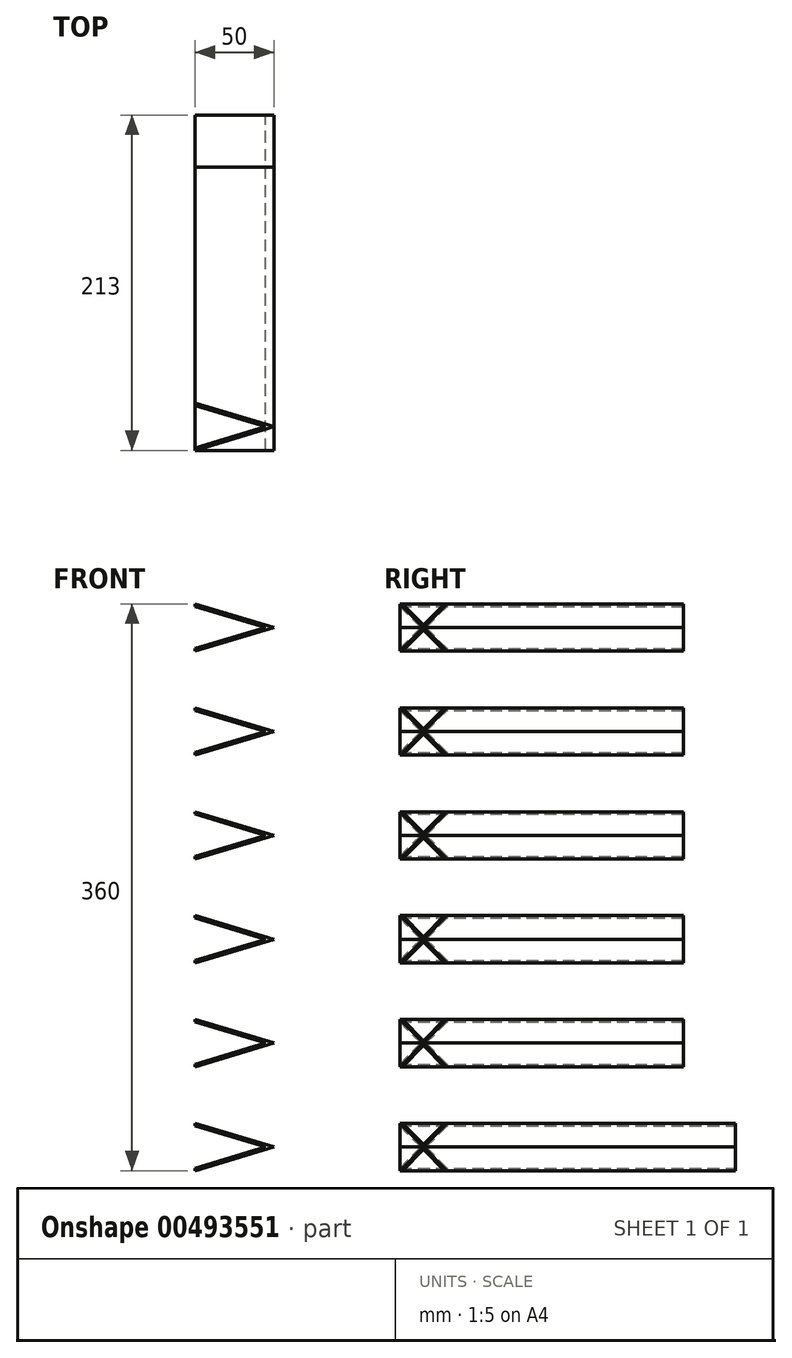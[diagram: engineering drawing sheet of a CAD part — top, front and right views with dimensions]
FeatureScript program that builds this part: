
annotation { "Feature Type Name" : "Feature", "Feature Type Description" : "" }
export const myFeature = defineFeature(function(context is Context, id is Id, definition is map)
    precondition{}
    {
        {
            var Q0;
            Q0=qCreatedBy(makeId("Right.planeOp"),FACE);
            var sketch = newSketch(context, id + "F0", { "sketchPlane" : qUnion([Q0])});
            skLineSegment(sketch, "E0", {"start": v(0, 0) * mm, "end": v(0, 400) * mm});
            skLineSegment(sketch, "E1", {"start": v(0, 0) * mm, "end": v(100, 0) * mm});
            skLineSegment(sketch, "E2", {"start": v(100, 0) * mm, "end": v(100, 360) * mm});
            skLineSegment(sketch, "E3.bottom", {"start": v(100, 360) * mm, "end": v(130, 360) * mm});
            skLineSegment(sketch, "E3.top", {"start": v(100, 0) * mm, "end": v(130, 0) * mm});
            skLineSegment(sketch, "E3.left", {"start": v(100, 360) * mm, "end": v(100, 0) * mm});
            skLineSegment(sketch, "E3.right", {"start": v(130, 360) * mm, "end": v(130, 0) * mm});
            skLineSegment(sketch, "E4.bottom", {"start": v(130, 0) * mm, "end": v(280, 0) * mm});
            skLineSegment(sketch, "E4.top", {"start": v(100, 30) * mm, "end": v(280, 30) * mm});
            skLineSegment(sketch, "E4.left", {"start": v(130, 0) * mm, "end": v(130, 30) * mm});
            skLineSegment(sketch, "E4.right", {"start": v(280, 0) * mm, "end": v(280, 30) * mm});
            skLineSegment(sketch, "E5", {"start": v(280, 66) * mm, "end": v(130, 66) * mm});
            skLineSegment(sketch, "E6", {"start": v(280, 66) * mm, "end": v(280, 96) * mm});
            skLineSegment(sketch, "E7.bottom", {"start": v(280, 96) * mm, "end": v(130, 96) * mm});
            skLineSegment(sketch, "E7.left", {"start": v(280, 96) * mm, "end": v(280, 66) * mm});
            skLineSegment(sketch, "E7.right", {"start": v(130, 96) * mm, "end": v(130, 66) * mm});
            skLineSegment(sketch, "E8.0.1.0", {"start": v(280, 132) * mm, "end": v(130, 132) * mm});
            skLineSegment(sketch, "E8.0.1.1", {"start": v(280, 132) * mm, "end": v(280, 162) * mm});
            skLineSegment(sketch, "E8.0.1.2", {"start": v(130, 162) * mm, "end": v(130, 132) * mm});
            skLineSegment(sketch, "E8.0.1.3", {"start": v(280, 162) * mm, "end": v(130, 162) * mm});
            skLineSegment(sketch, "E8.0.1.4", {"start": v(280, 162) * mm, "end": v(280, 132) * mm});
            skLineSegment(sketch, "E8.0.1.5", {"start": v(280, 132) * mm, "end": v(130, 132) * mm});
            skLineSegment(sketch, "E8.0.2.0", {"start": v(280, 198) * mm, "end": v(130, 198) * mm});
            skLineSegment(sketch, "E8.0.2.1", {"start": v(280, 198) * mm, "end": v(280, 228) * mm});
            skLineSegment(sketch, "E8.0.2.2", {"start": v(130, 228) * mm, "end": v(130, 198) * mm});
            skLineSegment(sketch, "E8.0.2.3", {"start": v(280, 228) * mm, "end": v(130, 228) * mm});
            skLineSegment(sketch, "E8.0.2.4", {"start": v(280, 228) * mm, "end": v(280, 198) * mm});
            skLineSegment(sketch, "E8.0.2.5", {"start": v(280, 198) * mm, "end": v(130, 198) * mm});
            skLineSegment(sketch, "E8.0.3.0", {"start": v(280, 264) * mm, "end": v(130, 264) * mm});
            skLineSegment(sketch, "E8.0.3.1", {"start": v(280, 264) * mm, "end": v(280, 294) * mm});
            skLineSegment(sketch, "E8.0.3.2", {"start": v(130, 294) * mm, "end": v(130, 264) * mm});
            skLineSegment(sketch, "E8.0.3.3", {"start": v(280, 294) * mm, "end": v(130, 294) * mm});
            skLineSegment(sketch, "E8.0.3.4", {"start": v(280, 294) * mm, "end": v(280, 264) * mm});
            skLineSegment(sketch, "E8.0.3.5", {"start": v(280, 264) * mm, "end": v(130, 264) * mm});
            skLineSegment(sketch, "E8.0.4.0", {"start": v(280, 330) * mm, "end": v(100, 330) * mm});
            skLineSegment(sketch, "E8.0.4.1", {"start": v(280, 330) * mm, "end": v(280, 360) * mm});
            skLineSegment(sketch, "E8.0.4.2", {"start": v(130, 360) * mm, "end": v(130, 330) * mm});
            skLineSegment(sketch, "E8.0.4.3", {"start": v(280, 360) * mm, "end": v(130, 360) * mm});
            skLineSegment(sketch, "E8.0.4.4", {"start": v(280, 360) * mm, "end": v(280, 330) * mm});
            skLineSegment(sketch, "E8.0.4.5", {"start": v(280, 330) * mm, "end": v(130, 330) * mm});
            skLineSegment(sketch, "E8.direction1", {"start": v(130, 66) * mm, "end": v(205, 66) * mm, "construction": true});
            skLineSegment(sketch, "E8.direction2", {"start": v(130, 66) * mm, "end": v(130, 132) * mm, "construction": true});
            skLineSegment(sketch, "E9", {"start": v(-100, 363) * mm, "end": v(-283, 363) * mm});
            skLineSegment(sketch, "E10", {"start": v(-100, 363) * mm, "end": v(-100, 393) * mm});
            skLineSegment(sketch, "E11.bottom", {"start": v(-283, 363) * mm, "end": v(-100, 363) * mm});
            skLineSegment(sketch, "E11.top", {"start": v(-313, 393) * mm, "end": v(-100, 393) * mm});
            skLineSegment(sketch, "E12.MirrorCS", {"start": v(-100, -3) * mm, "end": v(-100, -33) * mm});
            skLineSegment(sketch, "E13.MirrorCS", {"start": v(-283, -3) * mm, "end": v(-100, -3) * mm});
            skLineSegment(sketch, "E14.MirrorCS", {"start": v(-100, -3) * mm, "end": v(-283, -3) * mm});
            skLineSegment(sketch, "E15.MirrorCS", {"start": v(-313, -33) * mm, "end": v(-100, -33) * mm});
            skLineSegment(sketch, "E16", {"start": v(-283, 363) * mm, "end": v(-283, 327) * mm});
            skLineSegment(sketch, "E17.0", {"start": v(-133, 297) * mm, "end": v(-283, 297) * mm});
            skLineSegment(sketch, "E18.0", {"start": v(-133, 327) * mm, "end": v(-283, 327) * mm});
            skLineSegment(sketch, "E19.0", {"start": v(-313, 393) * mm, "end": v(-313, -33) * mm});
            skLineSegment(sketch, "E20.0", {"start": v(-133, 327) * mm, "end": v(-133, 297) * mm});
            skLineSegment(sketch, "E21.0.1.1", {"start": v(-133, 261) * mm, "end": v(-283, 261) * mm});
            skLineSegment(sketch, "E21.0.1.2", {"start": v(-133, 231) * mm, "end": v(-283, 231) * mm});
            skLineSegment(sketch, "E21.0.1.3", {"start": v(-133, 261) * mm, "end": v(-133, 231) * mm});
            skLineSegment(sketch, "E21.0.2.1", {"start": v(-133, 195) * mm, "end": v(-283, 195) * mm});
            skLineSegment(sketch, "E21.0.2.2", {"start": v(-133, 165) * mm, "end": v(-283, 165) * mm});
            skLineSegment(sketch, "E21.0.2.3", {"start": v(-133, 195) * mm, "end": v(-133, 165) * mm});
            skLineSegment(sketch, "E21.0.3.1", {"start": v(-133, 129) * mm, "end": v(-283, 129) * mm});
            skLineSegment(sketch, "E21.0.3.2", {"start": v(-133, 99) * mm, "end": v(-283, 99) * mm});
            skLineSegment(sketch, "E21.0.3.3", {"start": v(-133, 129) * mm, "end": v(-133, 99) * mm});
            skLineSegment(sketch, "E21.0.4.1", {"start": v(-133, 63) * mm, "end": v(-283, 63) * mm});
            skLineSegment(sketch, "E21.0.4.2", {"start": v(-133, 33) * mm, "end": v(-283, 33) * mm});
            skLineSegment(sketch, "E21.0.4.3", {"start": v(-133, 63) * mm, "end": v(-133, 33) * mm});
            skLineSegment(sketch, "E21.direction1", {"start": v(-283, 297) * mm, "end": v(-258, 297) * mm, "construction": true});
            skLineSegment(sketch, "E21.direction2", {"start": v(-283, 297) * mm, "end": v(-283, 261) * mm, "construction": true});
            skLineSegment(sketch, "E22.trimOffspring", {"start": v(-283, 297) * mm, "end": v(-283, 261) * mm});
            skLineSegment(sketch, "E23.trimOffspring", {"start": v(-283, 231) * mm, "end": v(-283, 195) * mm});
            skLineSegment(sketch, "E24.trimOffspring", {"start": v(-283, 165) * mm, "end": v(-283, 129) * mm});
            skLineSegment(sketch, "E25.trimOffspring", {"start": v(-283, 99) * mm, "end": v(-283, 63) * mm});
            skLineSegment(sketch, "E26.trimOffspring", {"start": v(-283, 33) * mm, "end": v(-283, -3) * mm});
            skLineSegment(sketch, "E27.MirrorCS", {"start": v(-280, 360) * mm, "end": v(-280, 330) * mm});
            skLineSegment(sketch, "E28.MirrorCS", {"start": v(-280, 330) * mm, "end": v(-280, 360) * mm});
            skLineSegment(sketch, "E29.MirrorCS", {"start": v(-280, 264) * mm, "end": v(-280, 294) * mm});
            skLineSegment(sketch, "E30.MirrorCS", {"start": v(-130, 360) * mm, "end": v(-130, 330) * mm});
            skLineSegment(sketch, "E31.MirrorCS", {"start": v(-280, 132) * mm, "end": v(-130, 132) * mm});
            skLineSegment(sketch, "E32.MirrorCS", {"start": v(-280, 330) * mm, "end": v(-130, 330) * mm});
            skLineSegment(sketch, "E33.MirrorCS", {"start": v(-100, 0) * mm, "end": v(-100, 360) * mm});
            skLineSegment(sketch, "E34.MirrorCS", {"start": v(-280, 66) * mm, "end": v(-130, 66) * mm});
            skLineSegment(sketch, "E35.MirrorCS", {"start": v(-280, 96) * mm, "end": v(-280, 66) * mm});
            skLineSegment(sketch, "E36.MirrorCS", {"start": v(-130, 96) * mm, "end": v(-130, 66) * mm});
            skLineSegment(sketch, "E37.MirrorCS", {"start": v(-280, 132) * mm, "end": v(-280, 162) * mm});
            skLineSegment(sketch, "E38.MirrorCS", {"start": v(-280, 264) * mm, "end": v(-130, 264) * mm});
            skLineSegment(sketch, "E39.MirrorCS", {"start": v(-280, 198) * mm, "end": v(-130, 198) * mm});
            skLineSegment(sketch, "E40.MirrorCS", {"start": v(-130, 228) * mm, "end": v(-130, 198) * mm});
            skLineSegment(sketch, "E41.MirrorCS", {"start": v(-280, 228) * mm, "end": v(-280, 198) * mm});
            skLineSegment(sketch, "E42.MirrorCS", {"start": v(-280, 66) * mm, "end": v(-280, 96) * mm});
            skLineSegment(sketch, "E43.MirrorCS", {"start": v(-280, 0) * mm, "end": v(-280, 30) * mm});
            skLineSegment(sketch, "E44.MirrorCS", {"start": v(-280, 294) * mm, "end": v(-280, 264) * mm});
            skLineSegment(sketch, "E45.MirrorCS", {"start": v(-130, 0) * mm, "end": v(-130, 30) * mm});
            skLineSegment(sketch, "E46.MirrorCS", {"start": v(-100, 30) * mm, "end": v(-280, 30) * mm});
            skLineSegment(sketch, "E47.MirrorCS", {"start": v(-130, 162) * mm, "end": v(-130, 132) * mm});
            skLineSegment(sketch, "E48.MirrorCS", {"start": v(-280, 330) * mm, "end": v(-100, 330) * mm});
            skLineSegment(sketch, "E49.MirrorCS", {"start": v(-130, 294) * mm, "end": v(-130, 264) * mm});
            skLineSegment(sketch, "E50.MirrorCS", {"start": v(-130, 0) * mm, "end": v(-280, 0) * mm});
            skLineSegment(sketch, "E51.MirrorCS", {"start": v(-130, 360) * mm, "end": v(-130, 0) * mm});
            skLineSegment(sketch, "E52.MirrorCS", {"start": v(-280, 162) * mm, "end": v(-280, 132) * mm});
            skLineSegment(sketch, "E53.MirrorCS", {"start": v(-280, 360) * mm, "end": v(-130, 360) * mm});
            skLineSegment(sketch, "E54.MirrorCS", {"start": v(-100, 360) * mm, "end": v(-100, 0) * mm});
            skLineSegment(sketch, "E55.MirrorCS", {"start": v(-100, 0) * mm, "end": v(-130, 0) * mm});
            skLineSegment(sketch, "E56.MirrorCS", {"start": v(-100, 360) * mm, "end": v(-130, 360) * mm});
            skLineSegment(sketch, "E57.MirrorCS", {"start": v(-280, 198) * mm, "end": v(-280, 228) * mm});
            skLineSegment(sketch, "E58.MirrorCS", {"start": v(-130, 66) * mm, "end": v(-130, 132) * mm, "construction": true});
            skLineSegment(sketch, "E59.MirrorCS", {"start": v(-280, 228) * mm, "end": v(-130, 228) * mm});
            skLineSegment(sketch, "E60.MirrorCS", {"start": v(-280, 96) * mm, "end": v(-130, 96) * mm});
            skLineSegment(sketch, "E61.MirrorCS", {"start": v(-280, 294) * mm, "end": v(-130, 294) * mm});
            skLineSegment(sketch, "E62.MirrorCS", {"start": v(-280, 162) * mm, "end": v(-130, 162) * mm});
            skLineSegment(sketch, "E63.MirrorCS", {"start": v(-130, 66) * mm, "end": v(-205, 66) * mm, "construction": true});
            skSolve(sketch);
        }
        {
            var Q0;
            Q0 = qSketchRegion(id + "F0", true);
            extrude(context, id + "F1", {"entities" : qUnion([Q0]), "endBound" : BoundingType.SYMMETRIC, "depth" : 50 * mm, "offsetDistance" : 25 * mm});
        }
        {
            var Q0;
            Q0=makeQuery(id+"F1.opExtrude","SWEPT_FACE",FACE,{"disambiguationData":[OSD([sQuery(id+"F0.wireOp",EDGE,"E10")])]});
            var sketch = newSketch(context, id + "F2", { "sketchPlane" : qUnion([Q0])});
            skLineSegment(sketch, "E64", {"start": v(-25, 378) * mm, "end": v(25, 393) * mm});
            skLineSegment(sketch, "E65", {"start": v(25, 393) * mm, "end": v(-25, 378) * mm});
            skLineSegment(sketch, "E66", {"start": v(25, 363) * mm, "end": v(-25, 378) * mm});
            skLineSegment(sketch, "E67.0", {"start": v(25.43, 364.44) * mm, "end": v(-19.78, 378) * mm});
            skLineSegment(sketch, "E68.trimOffspring", {"start": v(-19.78, 378) * mm, "end": v(25.43, 391.56) * mm});
            skSolve(sketch);
        }
        {
            var Q0;
            Q0=makeQuery(id+"F1.opExtrude","SWEPT_FACE",FACE,{"disambiguationData":[OSD([sQuery(id+"F0.wireOp",EDGE,"E11.top")])]});
            var sketch = newSketch(context, id + "F3", { "sketchPlane" : qUnion([Q0])});
            skLineSegment(sketch, "E69", {"start": v(25, -298) * mm, "end": v(-25, -313) * mm});
            skLineSegment(sketch, "E70", {"start": v(25, -298) * mm, "end": v(-25, -283) * mm});
            skLineSegment(sketch, "E71.trimOffspring", {"start": v(19.78, -298) * mm, "end": v(-25.43, -284.44) * mm});
            skLineSegment(sketch, "E72.trimOffspring", {"start": v(19.78, -298) * mm, "end": v(-25.43, -311.56) * mm});
            skSolve(sketch);
        }
        {
            var Q0;
            Q0=makeQuery(id+"F1.opExtrude","SWEPT_FACE",FACE,{"disambiguationData":[OSD([sQuery(id+"F0.wireOp",EDGE,"E20.0")])]});
            var sketch = newSketch(context, id + "F4", { "sketchPlane" : qUnion([Q0])});
            skLineSegment(sketch, "E73", {"start": v(-25, 312) * mm, "end": v(25, 327) * mm});
            skLineSegment(sketch, "E74", {"start": v(-25, 312) * mm, "end": v(25, 297) * mm});
            skLineSegment(sketch, "E75.trimOffspring", {"start": v(-19.78, 312) * mm, "end": v(25.43, 298.44) * mm});
            skLineSegment(sketch, "E76.trimOffspring", {"start": v(-19.78, 312) * mm, "end": v(25.43, 325.56) * mm});
            skSolve(sketch);
        }
        {
            var Q0;
            {var subQ8=sQuery(id+"F3.wireOp",EDGE,"E69");Q0=makeQuery(id+"F3.imprint","IMPRINT",FACE,{"disambiguationData":[TD([[makeQuery(id+"F3.imprint","IMPRINT",EDGE,{"derivedFrom":subQ8}),-1.0]])]});}
            var Q1;
            Q1=makeQuery(id+"F1.opExtrude","SWEPT_FACE",FACE,{"disambiguationData":[OSD([sQuery(id+"F0.wireOp",EDGE,"E15.MirrorCS")])]});
            extrude(context, id + "F5", {"entities" : qUnion([Q0]), "endBound" : BoundingType.UP_TO_SURFACE, "oppositeDirection" : true, "depth" : 25 * mm, "endBoundEntityFace" : qUnion([Q1]), "offsetDistance" : 25 * mm});
        }
        {
            var Q0;
            Q0=makeQuery(id+"F1.opExtrude","SWEPT_FACE",FACE,{"disambiguationData":[OSD([sQuery(id+"F0.wireOp",EDGE,"E21.0.1.3")])]});
            var sketch = newSketch(context, id + "F6", { "sketchPlane" : qUnion([Q0])});
            skLineSegment(sketch, "E77", {"start": v(-25, 246) * mm, "end": v(25, 261) * mm});
            skLineSegment(sketch, "E78", {"start": v(-25, 246) * mm, "end": v(25, 231) * mm});
            skLineSegment(sketch, "E79.0", {"start": v(-19.78, 246) * mm, "end": v(25.43, 259.56) * mm});
            skLineSegment(sketch, "E80.0", {"start": v(-19.78, 246) * mm, "end": v(25.43, 232.44) * mm});
            skSolve(sketch);
        }
        {
            var Q0;
            Q0=makeQuery(id+"F1.opExtrude","SWEPT_FACE",FACE,{"disambiguationData":[OSD([sQuery(id+"F0.wireOp",EDGE,"E21.0.2.3")])]});
            var sketch = newSketch(context, id + "F7", { "sketchPlane" : qUnion([Q0])});
            skLineSegment(sketch, "E81", {"start": v(-25, 180) * mm, "end": v(25, 195) * mm});
            skLineSegment(sketch, "E82", {"start": v(-25, 180) * mm, "end": v(25, 165) * mm});
            skLineSegment(sketch, "E83.0", {"start": v(-19.78, 180) * mm, "end": v(25.43, 193.56) * mm});
            skLineSegment(sketch, "E84.0", {"start": v(-19.78, 180) * mm, "end": v(25.43, 166.44) * mm});
            skSolve(sketch);
        }
        {
            var Q0;
            Q0=makeQuery(id+"F1.opExtrude","SWEPT_FACE",FACE,{"disambiguationData":[OSD([sQuery(id+"F0.wireOp",EDGE,"E21.0.3.3")])]});
            var sketch = newSketch(context, id + "F8", { "sketchPlane" : qUnion([Q0])});
            skLineSegment(sketch, "E85", {"start": v(25, 129) * mm, "end": v(-25, 114) * mm});
            skLineSegment(sketch, "E86", {"start": v(-25, 114) * mm, "end": v(25, 99) * mm});
            skLineSegment(sketch, "E87.0", {"start": v(25.43, 127.56) * mm, "end": v(-19.78, 114) * mm});
            skLineSegment(sketch, "E88.0", {"start": v(-19.78, 114) * mm, "end": v(25.43, 100.44) * mm});
            skSolve(sketch);
        }
        {
            var Q0;
            Q0=makeQuery(id+"F1.opExtrude","SWEPT_FACE",FACE,{"disambiguationData":[OSD([sQuery(id+"F0.wireOp",EDGE,"E21.0.4.3")])]});
            var sketch = newSketch(context, id + "F9", { "sketchPlane" : qUnion([Q0])});
            skLineSegment(sketch, "E89", {"start": v(25, 63) * mm, "end": v(-25, 48) * mm});
            skLineSegment(sketch, "E90", {"start": v(-25, 48) * mm, "end": v(25, 33) * mm});
            skLineSegment(sketch, "E91.0", {"start": v(25.43, 61.56) * mm, "end": v(-19.78, 48) * mm});
            skLineSegment(sketch, "E92.0", {"start": v(-19.78, 48) * mm, "end": v(25.43, 34.44) * mm});
            skSolve(sketch);
        }
        {
            var Q0;
            Q0=makeQuery(id+"F1.opExtrude","SWEPT_FACE",FACE,{"disambiguationData":[OSD([sQuery(id+"F0.wireOp",EDGE,"E12.MirrorCS")])]});
            var sketch = newSketch(context, id + "F10", { "sketchPlane" : qUnion([Q0])});
            skLineSegment(sketch, "E93", {"start": v(25, -3) * mm, "end": v(-25, -18) * mm});
            skLineSegment(sketch, "E94", {"start": v(-25, -18) * mm, "end": v(25, -33) * mm});
            skLineSegment(sketch, "E95.0", {"start": v(25.43, -4.44) * mm, "end": v(-19.78, -18) * mm});
            skLineSegment(sketch, "E96.0", {"start": v(-19.78, -18) * mm, "end": v(25.43, -31.56) * mm});
            skSolve(sketch);
        }
        {
            var Q0;
            {var subQ8=sQuery(id+"F2.wireOp",EDGE,"E65");Q0=makeQuery(id+"F2.imprint","IMPRINT",FACE,{"disambiguationData":[TD([[makeQuery(id+"F2.imprint","IMPRINT",EDGE,{"derivedFrom":subQ8}),1.0]])]});}
            var Q1;
            {var subQ8=sQuery(id+"F4.wireOp",EDGE,"E73");Q1=makeQuery(id+"F4.imprint","IMPRINT",FACE,{"disambiguationData":[TD([[makeQuery(id+"F4.imprint","IMPRINT",EDGE,{"derivedFrom":subQ8}),-1.0]])]});}
            var Q2;
            {var subQ8=sQuery(id+"F6.wireOp",EDGE,"E77");Q2=makeQuery(id+"F6.imprint","IMPRINT",FACE,{"disambiguationData":[TD([[makeQuery(id+"F6.imprint","IMPRINT",EDGE,{"derivedFrom":subQ8}),-1.0]])]});}
            var Q3;
            {var subQ8=sQuery(id+"F7.wireOp",EDGE,"E81");Q3=makeQuery(id+"F7.imprint","IMPRINT",FACE,{"disambiguationData":[TD([[makeQuery(id+"F7.imprint","IMPRINT",EDGE,{"derivedFrom":subQ8}),-1.0]])]});}
            var Q4;
            {var subQ8=sQuery(id+"F8.wireOp",EDGE,"E85");Q4=makeQuery(id+"F8.imprint","IMPRINT",FACE,{"disambiguationData":[TD([[makeQuery(id+"F8.imprint","IMPRINT",EDGE,{"derivedFrom":subQ8}),1.0]])]});}
            var Q5;
            {var subQ8=sQuery(id+"F9.wireOp",EDGE,"E89");Q5=makeQuery(id+"F9.imprint","IMPRINT",FACE,{"disambiguationData":[TD([[makeQuery(id+"F9.imprint","IMPRINT",EDGE,{"derivedFrom":subQ8}),1.0]])]});}
            var Q6;
            {var subQ8=sQuery(id+"F10.wireOp",EDGE,"E93");Q6=makeQuery(id+"F10.imprint","IMPRINT",FACE,{"disambiguationData":[TD([[makeQuery(id+"F10.imprint","IMPRINT",EDGE,{"derivedFrom":subQ8}),1.0]])]});}
            var Q7;
            Q7=makeQuery(id+"F1.opExtrude","SWEPT_FACE",FACE,{"disambiguationData":[OSD([sQuery(id+"F0.wireOp",EDGE,"E19.0")])]});
            var Q8;
            Q8=makeQuery(id+"F5.opExtrude","CAP_VERTEX",VERTEX,{"disambiguationData":[OSD([sQuery(id+"F0.wireOp",EDGE,"E11.top"),sQuery(id+"F3.wireOp",EDGE,"E69"),sQuery(id+"F3.wireOp",EDGE,"E70")])],"isStart":true});
            extrude(context, id + "F11", {"entities" : qUnion([Q0, Q1, Q2, Q3, Q4, Q5, Q6]), "operationType" : NewBodyOperationType.INTERSECT, "endBound" : BoundingType.UP_TO_SURFACE, "oppositeDirection" : true, "depth" : 25 * mm, "endBoundEntityFace" : qUnion([Q7]), "endBoundEntityVertex" : qUnion([Q8]), "offsetDistance" : 25 * mm});
        }
    });
